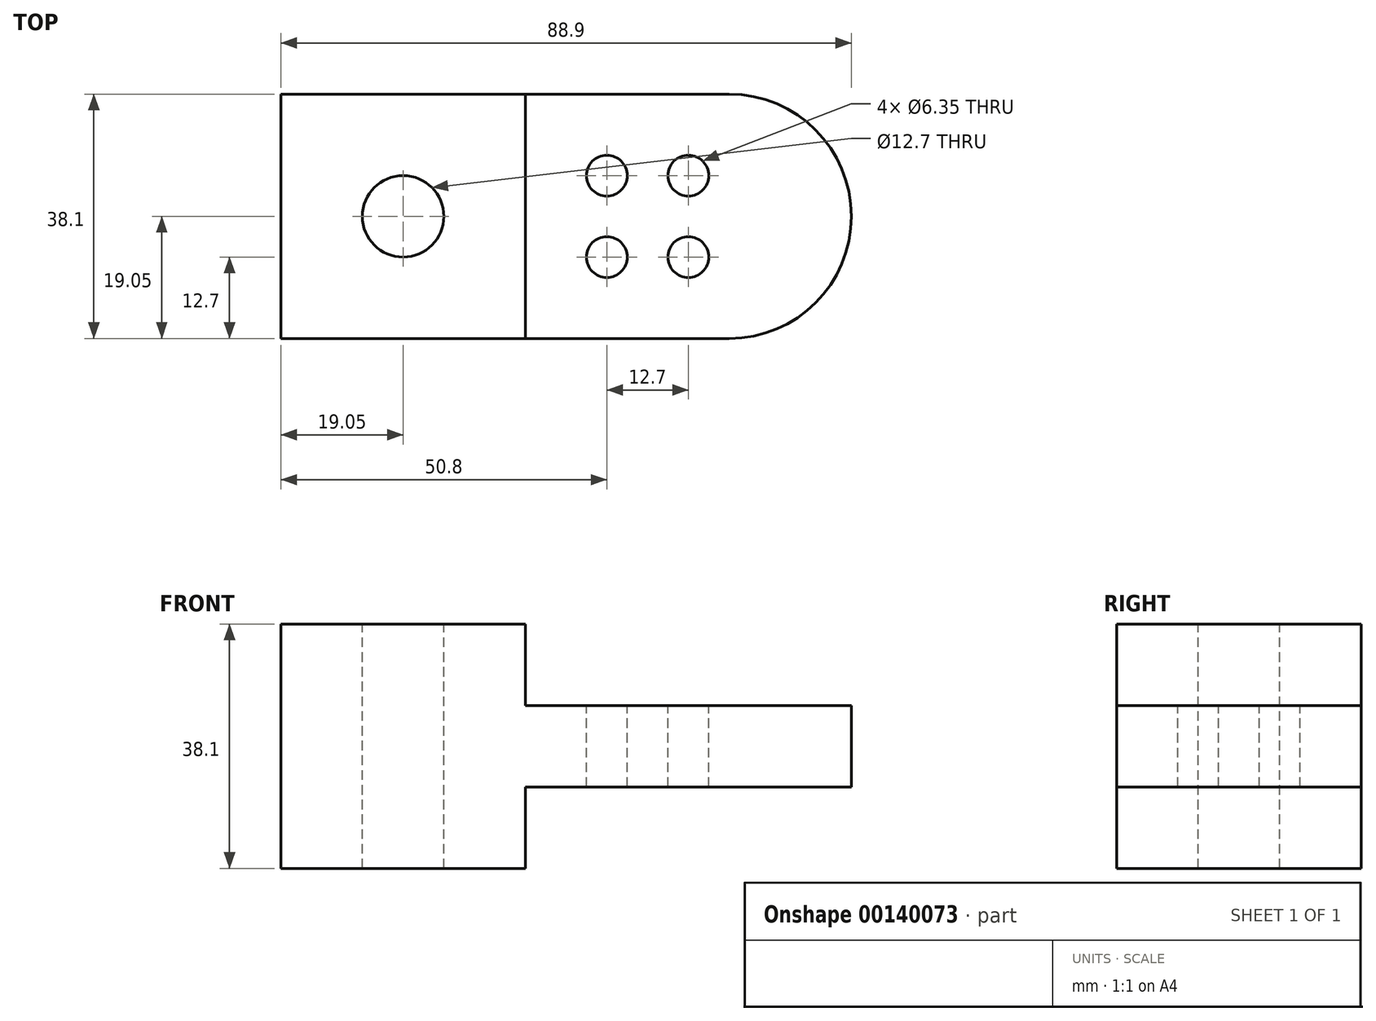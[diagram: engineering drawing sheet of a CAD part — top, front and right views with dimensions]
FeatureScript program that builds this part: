
annotation { "Feature Type Name" : "Feature", "Feature Type Description" : "" }
export const myFeature = defineFeature(function(context is Context, id is Id, definition is map)
    precondition{}
    {
        {
            var Q0;
            Q0=qCreatedBy(makeId("Top.planeOp"),FACE);
            var sketch = newSketch(context, id + "F0", { "sketchPlane" : qUnion([Q0])});
            skLineSegment(sketch, "E0", {"start": v(0, 0) * mm, "end": v(0, 38.1) * mm});
            skLineSegment(sketch, "E1", {"start": v(0, 38.1) * mm, "end": v(38.1, 38.1) * mm});
            skLineSegment(sketch, "E2", {"start": v(38.1, 38.1) * mm, "end": v(38.1, 0) * mm});
            skLineSegment(sketch, "E3", {"start": v(38.1, 0) * mm, "end": v(0, 0) * mm});
            skLineSegment(sketch, "E4", {"start": v(38.1, 38.1) * mm, "end": v(69.85, 38.1) * mm});
            skArc(sketch, "E5", {"start": v(69.85, 0) * mm, "mid": v(88.9, 19.05) * mm, "end": v(69.85, 38.1) * mm});
            skLineSegment(sketch, "E6", {"start": v(69.85, 0) * mm, "end": v(38.1, 0) * mm});
            skSolve(sketch);
        }
        {
            var Q0;
            Q0=makeQuery(id+"F0.imprint","IMPRINT",FACE,{"disambiguationData":[TD([[makeQuery(id+"F0.imprint","IMPRINT",EDGE,{"derivedFrom":sQuery(id+"F0.wireOp",EDGE,"E0")}),-1.0]])]});
            extrude(context, id + "F1", {"entities" : qUnion([Q0]), "endBound" : BoundingType.SYMMETRIC, "depth" : 38.1 * mm});
        }
        {
            var Q0;
            Q0=makeQuery(id+"F0.imprint","IMPRINT",FACE,{"disambiguationData":[TD([[makeQuery(id+"F0.imprint","IMPRINT",EDGE,{"derivedFrom":sQuery(id+"F0.wireOp",EDGE,"E2")}),1.0]])]});
            extrude(context, id + "F2", {"entities" : qUnion([Q0]), "operationType" : NewBodyOperationType.ADD, "endBound" : BoundingType.SYMMETRIC, "depth" : 12.7 * mm});
        }
        {
            var Q0;
            Q0=makeQuery(id+"F1.opExtrude","CAP_FACE",FACE,{"disambiguationData":[OSD([sQuery(id+"F0.wireOp",EDGE,"E0"),sQuery(id+"F0.wireOp",EDGE,"E1"),sQuery(id+"F0.wireOp",EDGE,"E2"),sQuery(id+"F0.wireOp",EDGE,"E3")])],"isStart":false});
            var sketch = newSketch(context, id + "F3", { "sketchPlane" : qUnion([Q0])});
            skCircle(sketch, "E7", {"center": v(19.05, 19.05) * mm, "radius": 6.35 * mm});
            skSolve(sketch);
        }
        {
            var Q0;
            Q0=makeQuery(id+"F3.imprint","IMPRINT",FACE,{"disambiguationData":[TD([[makeQuery(id+"F3.imprint","IMPRINT",EDGE,{"derivedFrom":sQuery(id+"F3.wireOp",EDGE,"E7")}),1.0]])]});
            extrude(context, id + "F4", {"entities" : qUnion([Q0]), "operationType" : NewBodyOperationType.REMOVE, "endBound" : BoundingType.THROUGH_ALL, "oppositeDirection" : true, "depth" : 25.4 * mm});
        }
        {
            var Q0;
            Q0=makeQuery(id+"F2.opExtrude","CAP_FACE",FACE,{"disambiguationData":[OSD([sQuery(id+"F0.wireOp",EDGE,"E2"),sQuery(id+"F0.wireOp",EDGE,"E4"),sQuery(id+"F0.wireOp",EDGE,"E5"),sQuery(id+"F0.wireOp",EDGE,"E6")])],"isStart":false});
            var sketch = newSketch(context, id + "F5", { "sketchPlane" : qUnion([Q0])});
            skCircle(sketch, "E8", {"center": v(50.8, 12.7) * mm, "radius": 3.18 * mm});
            skCircle(sketch, "E9", {"center": v(50.8, 25.4) * mm, "radius": 3.18 * mm});
            skCircle(sketch, "E10", {"center": v(63.5, 25.4) * mm, "radius": 3.18 * mm});
            skCircle(sketch, "E11", {"center": v(63.5, 12.7) * mm, "radius": 3.18 * mm});
            skSolve(sketch);
        }
        {
            var Q0;
            Q0 = qSketchRegion(id + "F5", true);
            extrude(context, id + "F6", {"entities" : qUnion([Q0]), "operationType" : NewBodyOperationType.REMOVE, "oppositeDirection" : true, "depth" : 25.4 * mm});
        }
    });
